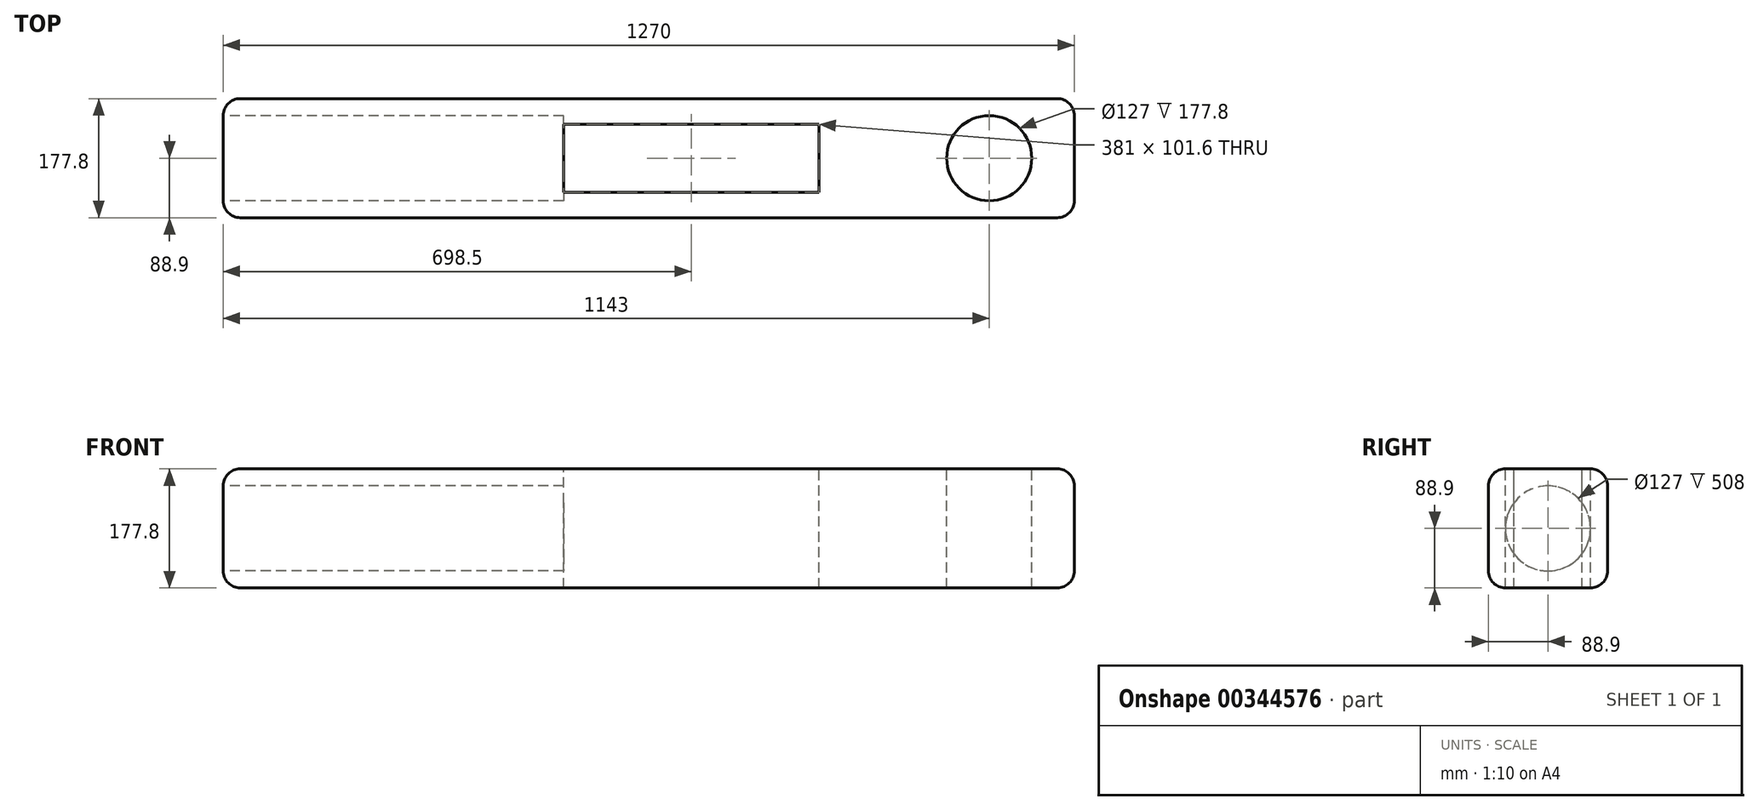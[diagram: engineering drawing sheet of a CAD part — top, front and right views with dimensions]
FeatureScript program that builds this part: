
annotation { "Feature Type Name" : "Feature", "Feature Type Description" : "" }
export const myFeature = defineFeature(function(context is Context, id is Id, definition is map)
    precondition{}
    {
        {
            var Q0;
            Q0=qCreatedBy(makeId("Right.planeOp"),FACE);
            var sketch = newSketch(context, id + "F0", { "sketchPlane" : qUnion([Q0])});
            skLineSegment(sketch, "E0.bottom", {"start": v(-88.9, 88.9) * mm, "end": v(88.9, 88.9) * mm});
            skLineSegment(sketch, "E0.top", {"start": v(-88.9, -88.9) * mm, "end": v(88.9, -88.9) * mm});
            skLineSegment(sketch, "E0.left", {"start": v(-88.9, 88.9) * mm, "end": v(-88.9, -88.9) * mm});
            skLineSegment(sketch, "E0.right", {"start": v(88.9, 88.9) * mm, "end": v(88.9, -88.9) * mm});
            skPoint(sketch, "E0.middle", {"position": v(0, 0) * mm});
            skSolve(sketch);
        }
        {
            var Q0;
            Q0 = qSketchRegion(id + "F0", true);
            extrude(context, id + "F1", {"entities" : qUnion([Q0]), "depth" : 1270 * mm});
        }
        {
            var Q0;
            Q0=makeQuery(id+"F1.opExtrude","SWEPT_FACE",FACE,{"disambiguationData":[OSD([sQuery(id+"F0.wireOp",EDGE,"E0.bottom")])]});
            var sketch = newSketch(context, id + "F2", { "sketchPlane" : qUnion([Q0])});
            skCircle(sketch, "E1", {"center": v(1143, 0) * mm, "radius": 63.5 * mm});
            skSolve(sketch);
        }
        {
            var Q0;
            Q0=makeQuery(id+"F2.imprint","IMPRINT",FACE,{"disambiguationData":[TD([[makeQuery(id+"F2.imprint","IMPRINT",EDGE,{"derivedFrom":sQuery(id+"F2.wireOp",EDGE,"E1")}),1.0]])]});
            extrude(context, id + "F3", {"entities" : qUnion([Q0]), "operationType" : NewBodyOperationType.REMOVE, "oppositeDirection" : true, "depth" : 177.8 * mm});
        }
        {
            var Q0;
            Q0=makeQuery(id+"F1.opExtrude","CAP_FACE",FACE,{"disambiguationData":[OSD([sQuery(id+"F0.wireOp",EDGE,"E0.bottom"),sQuery(id+"F0.wireOp",EDGE,"E0.top"),sQuery(id+"F0.wireOp",EDGE,"E0.left"),sQuery(id+"F0.wireOp",EDGE,"E0.right")])],"isStart":true});
            var sketch = newSketch(context, id + "F4", { "sketchPlane" : qUnion([Q0])});
            skCircle(sketch, "E2", {"center": v(0, 0) * mm, "radius": 63.5 * mm});
            skSolve(sketch);
        }
        {
            var Q0;
            Q0 = qSketchRegion(id + "F4", true);
            extrude(context, id + "F5", {"entities" : qUnion([Q0]), "operationType" : NewBodyOperationType.REMOVE, "oppositeDirection" : true, "depth" : 508 * mm});
        }
        {
            var Q0;
            Q0=makeQuery(id+"F1.opExtrude","SWEPT_EDGE",EDGE,{"disambiguationData":[OSD([sQuery(id+"F0.wireOp",EDGE,"E0.bottom"),sQuery(id+"F0.wireOp",EDGE,"E0.left")])]});
            var Q1;
            Q1=makeQuery(id+"F1.opExtrude","SWEPT_EDGE",EDGE,{"disambiguationData":[OSD([sQuery(id+"F0.wireOp",EDGE,"E0.bottom"),sQuery(id+"F0.wireOp",EDGE,"E0.right")])]});
            var Q2;
            Q2=makeQuery(id+"F1.opExtrude","SWEPT_EDGE",EDGE,{"disambiguationData":[OSD([sQuery(id+"F0.wireOp",EDGE,"E0.top"),sQuery(id+"F0.wireOp",EDGE,"E0.left")])]});
            var Q3;
            Q3=makeQuery(id+"F1.opExtrude","SWEPT_EDGE",EDGE,{"disambiguationData":[OSD([sQuery(id+"F0.wireOp",EDGE,"E0.top"),sQuery(id+"F0.wireOp",EDGE,"E0.right")])]});
            fillet(context, id + "F6", {"entities" : qUnion([Q0, Q1, Q2, Q3]), "radius" : 25.4 * mm, "tangentPropagation" : true, "allowEdgeOverflow" : false});
        }
        {
            var Q0;
            Q0=makeQuery(id+"F1.opExtrude","CAP_EDGE",EDGE,{"disambiguationData":[OSD([sQuery(id+"F0.wireOp",EDGE,"E0.bottom")])],"isStart":false});
            fillet(context, id + "F7", {"entities" : qUnion([Q0]), "radius" : 25.4 * mm, "tangentPropagation" : true, "allowEdgeOverflow" : false});
        }
        {
            var Q0;
            Q0=makeQuery(id+"F1.opExtrude","SWEPT_FACE",FACE,{"disambiguationData":[OSD([sQuery(id+"F0.wireOp",EDGE,"E0.bottom")])]});
            var sketch = newSketch(context, id + "F8", { "sketchPlane" : qUnion([Q0])});
            skLineSegment(sketch, "E3.bottom", {"start": v(508, 50.8) * mm, "end": v(889, 50.8) * mm});
            skLineSegment(sketch, "E3.top", {"start": v(508, -50.8) * mm, "end": v(889, -50.8) * mm});
            skLineSegment(sketch, "E3.left", {"start": v(508, 50.8) * mm, "end": v(508, -50.8) * mm});
            skLineSegment(sketch, "E3.right", {"start": v(889, 50.8) * mm, "end": v(889, -50.8) * mm});
            skSolve(sketch);
        }
        {
            var Q0;
            Q0 = qSketchRegion(id + "F8", true);
            extrude(context, id + "F9", {"entities" : qUnion([Q0]), "operationType" : NewBodyOperationType.REMOVE, "oppositeDirection" : true, "depth" : 177.8 * mm});
        }
        {
            var Q0;
            Q0=makeQuery(id+"F1.opExtrude","CAP_EDGE",EDGE,{"disambiguationData":[OSD([sQuery(id+"F0.wireOp",EDGE,"E0.bottom")])],"isStart":true});
            fillet(context, id + "F10", {"entities" : qUnion([Q0]), "radius" : 25.4 * mm, "tangentPropagation" : true, "allowEdgeOverflow" : false});
        }
    });
